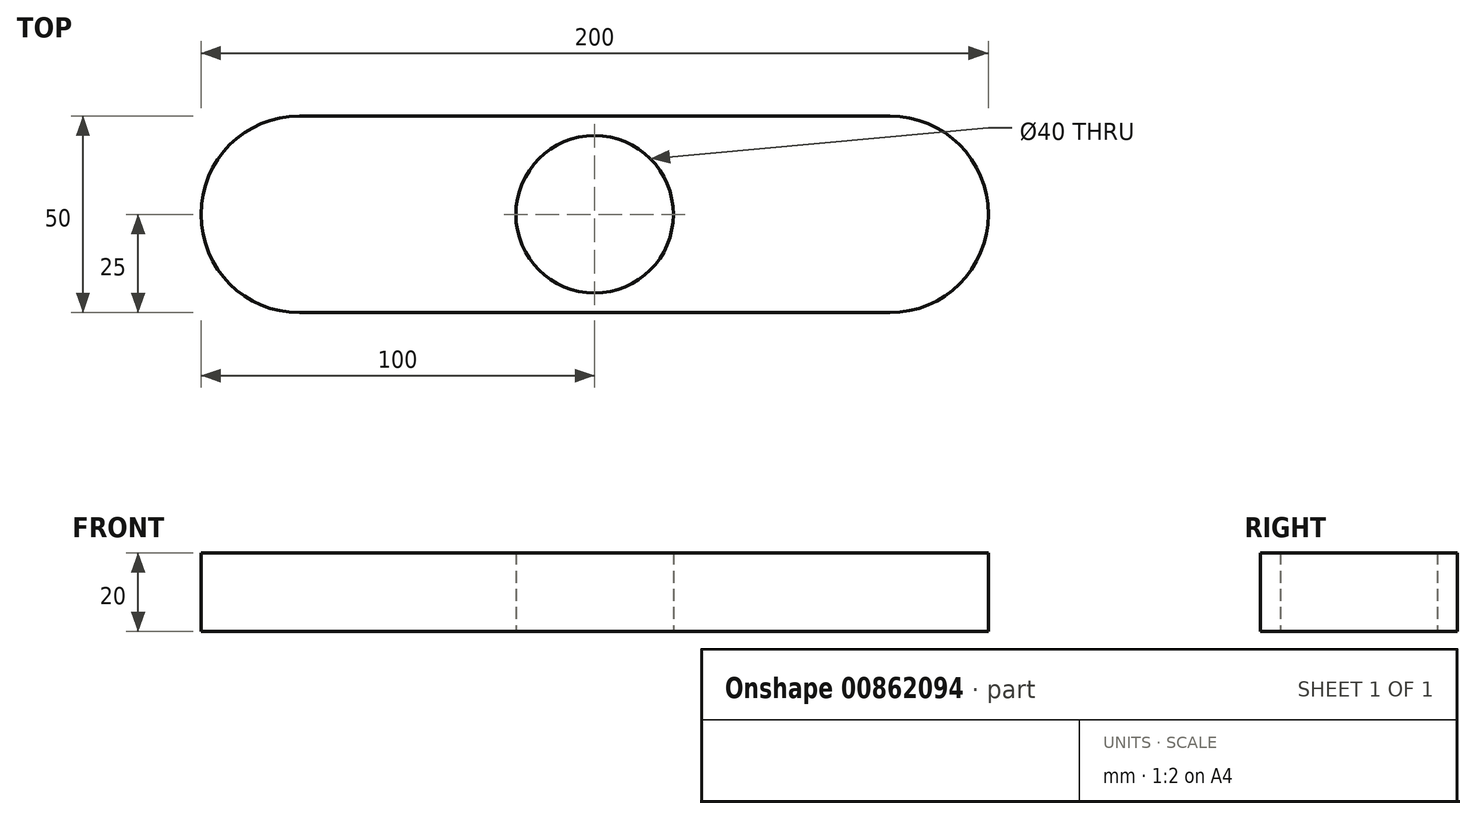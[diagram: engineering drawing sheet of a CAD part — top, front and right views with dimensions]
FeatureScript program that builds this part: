
annotation { "Feature Type Name" : "Feature", "Feature Type Description" : "" }
export const myFeature = defineFeature(function(context is Context, id is Id, definition is map)
    precondition{}
    {
        {
            var Q0;
            Q0=qCreatedBy(makeId("Top.planeOp"),FACE);
            var sketch = newSketch(context, id + "F0", { "sketchPlane" : qUnion([Q0])});
            skLineSegment(sketch, "E0.bottom", {"start": v(0, 50) * mm, "end": v(200, 50) * mm});
            skLineSegment(sketch, "E0.top", {"start": v(0, 0) * mm, "end": v(200, 0) * mm});
            skLineSegment(sketch, "E0.left", {"start": v(0, 50) * mm, "end": v(0, 0) * mm});
            skLineSegment(sketch, "E0.right", {"start": v(200, 50) * mm, "end": v(200, 0) * mm});
            skCircle(sketch, "E1", {"center": v(100, 25) * mm, "radius": 20 * mm});
            skLineSegment(sketch, "E2", {"start": v(0, 50) * mm, "end": v(200, 0) * mm, "construction": true});
            skSolve(sketch);
        }
        {
            var Q0;
            Q0=makeQuery(id+"F0.imprint","IMPRINT",FACE,{"disambiguationData":[TD([[makeQuery(id+"F0.imprint","IMPRINT",EDGE,{"derivedFrom":sQuery(id+"F0.wireOp",EDGE,"E0.bottom")}),-1.0]])]});
            extrude(context, id + "F1", {"entities" : qUnion([Q0]), "depth" : 20 * mm, "offsetDistance" : 25.4 * mm});
        }
        {
            var Q0;
            Q0=makeQuery(id+"F1.opExtrude","SWEPT_EDGE",EDGE,{"disambiguationData":[OSD([sQuery(id+"F0.wireOp",EDGE,"E0.top"),sQuery(id+"F0.wireOp",EDGE,"E0.right")])]});
            var Q1;
            Q1=makeQuery(id+"F1.opExtrude","SWEPT_EDGE",EDGE,{"disambiguationData":[OSD([sQuery(id+"F0.wireOp",EDGE,"E0.bottom"),sQuery(id+"F0.wireOp",EDGE,"E0.right")])]});
            var Q2;
            Q2=makeQuery(id+"F1.opExtrude","SWEPT_EDGE",EDGE,{"disambiguationData":[OSD([sQuery(id+"F0.wireOp",EDGE,"E0.bottom"),sQuery(id+"F0.wireOp",EDGE,"E0.left")])]});
            var Q3;
            Q3=makeQuery(id+"F1.opExtrude","SWEPT_EDGE",EDGE,{"disambiguationData":[OSD([sQuery(id+"F0.wireOp",EDGE,"E0.top"),sQuery(id+"F0.wireOp",EDGE,"E0.left")])]});
            fillet(context, id + "F2", {"entities" : qUnion([Q0, Q1, Q2, Q3]), "radius" : 25 * mm, "tangentPropagation" : true, "allowEdgeOverflow" : false});
        }
    });
